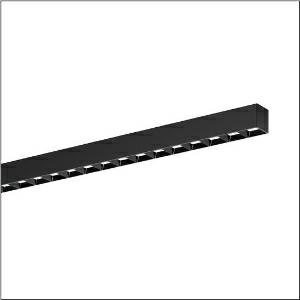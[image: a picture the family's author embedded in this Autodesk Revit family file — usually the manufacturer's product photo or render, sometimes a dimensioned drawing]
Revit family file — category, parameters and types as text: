
# Revit family: silica_r__21_51mx24tat4b_951d
name_source: partatom
category: Lighting Fixtures
units: mm (PartAtom-declared; Revit-internal decimal feet)

## family parameters
Cut with Voids When Loaded = No
Host = Face
Light Source = No
Part Type = Normal
Room Calculation Point = No
Round Connector Dimension = Use Diameter
Shared = No

## types (1)
- --- (1 x LED, 3280 lm, 32.4 W, 6500K)
    Apparent Load = 32 VA
    CIE Flux Codes = 74 94 99 100 100
    Color Rendering = 80
    Color Temperature = 6500K
    Default Elevation = 1800 mm
    Description = Silica® 21, office luminaire, primary light control with darklight reflector, of PMMA, black, light emission: direct distribution, primary light characteristic: asymmetric, installation type: surface-mounted, LED, rated luminous flux: 3.280lm, luminous efficacy: 96lm/W, light colour: 8tw, colour temperature: 2700..6500K, control gear: DALI DT8, with terminal, 3+2-pole, max. 2.5mm², mains connection: 220..240V, AC, 50/60Hz, rated input power: 34.1W, luminaire housing, of aluminium, matt jet black (RAL 9005), length: 1.204mm, width: 53mm, height: 53mm, protection rating (complete): IP20, insulation class (complete): insulation class I (protective earthing), certification: CE, permissible operating ambient temperature: 0..+35°C, standard: EN 50419, packaging unit: 1 piece
    Height = 53 mm
    Lamp = 1 x LED
    Lamp Light Flux = 3280 lm
    Lamp Power = 32.4 W
    Lamp count = 1
    Length = 1204 mm
    Luminous efficacy = 101 lm/W
    Manufacturer = Siteco
    ModVariant = No
    Model = 51MX24TAT4B
    Mounting Place = Ceiling
    Mounting Type = Surface mounted
    Number of Poles = 1
    OnlyDefault = Yes
    Power Factor = 1
    Product Name = Silica® 21
    Product group = office luminaire | ceiling mounted
    ProductGroupID = 302
    Protection Class = Protection class I
    Protection Degree = IP 20
    RLX_Detail_Level = 1
    RLX_Emergency_Light_Flux = 0 lm
    RLX_Emergency_Type = 0
    RLX_Emergency_Type_DB = No
    RlxData = <blob elided: 40565 chars, md5=05df2928>
    Socket = socket
    Standby Power = 0 W
    System Light Flux = 3280 lm
    System Power = 32 W
    Type Comments = individual setting
    Type Image = l_1335908.jpg
    URL = http://relux.com
    VarID = @adj_139998
    Voltage = 0 V
    Weight = 0.00 kg
    Width = 53 mm

## geometry (parser evidence)
native form markers: Blend x4, Sweep x11
no freeform markers — native parametric forms only
